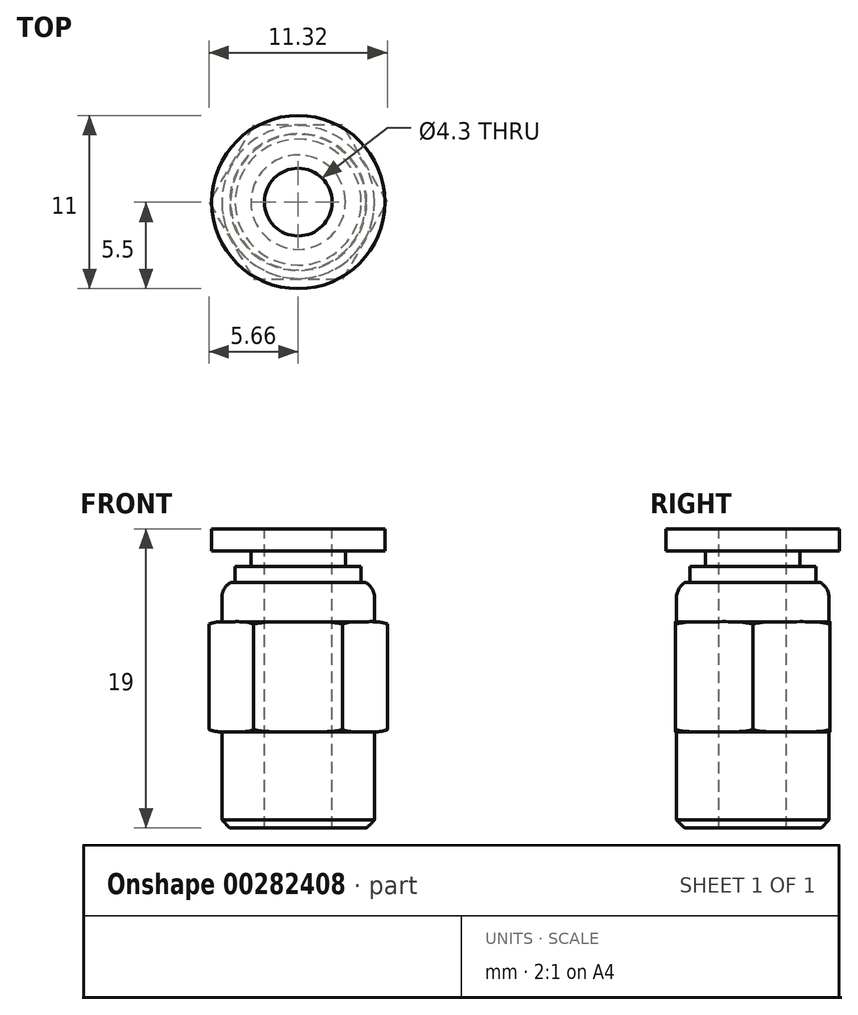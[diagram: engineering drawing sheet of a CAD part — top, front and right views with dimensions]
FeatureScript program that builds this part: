
annotation { "Feature Type Name" : "Feature", "Feature Type Description" : "" }
export const myFeature = defineFeature(function(context is Context, id is Id, definition is map)
    precondition{}
    {
        {
            var Q0;
            Q0=qCreatedBy(makeId("Front.planeOp"),FACE);
            var sketch = newSketch(context, id + "F0", { "sketchPlane" : qUnion([Q0])});
            skLineSegment(sketch, "E0", {"start": v(0, 0) * mm, "end": v(0, 19) * mm});
            skLineSegment(sketch, "E1", {"start": v(0, 19) * mm, "end": v(5.5, 19) * mm});
            skLineSegment(sketch, "E2", {"start": v(5.5, 19) * mm, "end": v(5.5, 17.6) * mm});
            skLineSegment(sketch, "E3", {"start": v(5.5, 17.6) * mm, "end": v(3, 17.6) * mm});
            skLineSegment(sketch, "E4", {"start": v(3, 17.6) * mm, "end": v(3, 16.6) * mm});
            skLineSegment(sketch, "E5", {"start": v(3, 16.6) * mm, "end": v(4, 16.6) * mm});
            skLineSegment(sketch, "E6", {"start": v(4, 16.6) * mm, "end": v(4, 15.6) * mm});
            skLineSegment(sketch, "E7", {"start": v(4, 15.6) * mm, "end": v(4.3, 15.6) * mm});
            skLineSegment(sketch, "E8", {"start": v(4.85, 14.6) * mm, "end": v(4.85, 13.1) * mm});
            skLineSegment(sketch, "E9", {"start": v(7, 11.6) * mm, "end": v(7, 7.6) * mm});
            skLineSegment(sketch, "E10", {"start": v(4.85, 6.1) * mm, "end": v(4.85, 0) * mm});
            skLineSegment(sketch, "E11", {"start": v(4.85, 0) * mm, "end": v(0, 0) * mm});
            skLineSegment(sketch, "E12", {"start": v(7, 9.6) * mm, "end": v(0, 9.6) * mm, "construction": true});
            skPoint(sketch, "E13.end.orphan", {"position": v(7, 13.1) * mm});
            skLineSegment(sketch, "E14", {"start": v(4.85, 13.1) * mm, "end": v(0, 13.1) * mm, "construction": true});
            skLineSegment(sketch, "E15", {"start": v(4.85, 6.1) * mm, "end": v(0, 6.1) * mm, "construction": true});
            skArc(sketch, "E16", {"start": v(7, 11.6) * mm, "mid": v(6.16, 12.69) * mm, "end": v(4.85, 13.1) * mm});
            skArc(sketch, "E17", {"start": v(4.85, 6.1) * mm, "mid": v(6.16, 6.51) * mm, "end": v(7, 7.6) * mm});
            skPoint(sketch, "E18.start.orphan", {"position": v(7, 6.1) * mm});
            skPoint(sketch, "E19.orphan", {"position": v(4.85, 15.6) * mm});
            skArc(sketch, "E20", {"start": v(4.85, 14.6) * mm, "mid": v(4.7, 15.17) * mm, "end": v(4.3, 15.6) * mm});
            skSolve(sketch);
        }
        {
            var Q0;
            Q0=qSketchRegion(id+"F0",true);
            var Q1;
            Q1=sQuery(id+"F0.wireOp",EDGE,"E0");
            revolve(context, id + "F1", {"entities" : qUnion([Q0]), "axis" : qUnion([Q1]), "revolveType" : RevolveType.FULL});
        }
        {
            var Q0;
            Q0=makeQuery(id+"F1.opRevolve","SWEPT_FACE",FACE,{"disambiguationData":[OSD([sQuery(id+"F0.wireOp",EDGE,"E1")])]});
            var sketch = newSketch(context, id + "F2", { "sketchPlane" : qUnion([Q0])});
            skCircle(sketch, "E21", {"center": v(0, 0) * mm, "radius": 2.15 * mm});
            skSolve(sketch);
        }
        {
            var Q0;
            Q0=qSketchRegion(id+"F2",true);
            extrude(context, id + "F3", {"entities" : qUnion([Q0]), "operationType" : NewBodyOperationType.REMOVE, "endBound" : BoundingType.THROUGH_ALL, "oppositeDirection" : true, "depth" : 25 * mm});
        }
        {
            var Q0;
            Q0=makeQuery(id+"F1.opRevolve","SWEPT_FACE",FACE,{"disambiguationData":[OSD([sQuery(id+"F0.wireOp",EDGE,"E11")])]});
            var sketch = newSketch(context, id + "F4", { "sketchPlane" : qUnion([Q0])});
            skCircle(sketch, "E22.cCircle", {"center": v(0, 0) * mm, "radius": 4.9 * mm, "construction": true});
            skLineSegment(sketch, "E22.0", {"start": v(2.83, 4.9) * mm, "end": v(5.66, 0) * mm});
            skLineSegment(sketch, "E22.1", {"start": v(5.66, 0) * mm, "end": v(2.83, -4.9) * mm});
            skLineSegment(sketch, "E22.2", {"start": v(2.83, -4.9) * mm, "end": v(-2.83, -4.9) * mm});
            skLineSegment(sketch, "E22.3", {"start": v(-2.83, -4.9) * mm, "end": v(-5.66, 0) * mm});
            skLineSegment(sketch, "E22.4", {"start": v(-5.66, 0) * mm, "end": v(-2.83, 4.9) * mm});
            skLineSegment(sketch, "E22.5", {"start": v(-2.83, 4.9) * mm, "end": v(2.83, 4.9) * mm});
            skPoint(sketch, "E22.0.midPoint", {"position": v(4.24, 2.45) * mm});
            skLineSegment(sketch, "E23", {"start": v(0, 0) * mm, "end": v(-5.66, 0) * mm, "construction": true});
            skCircle(sketch, "E24", {"center": v(0, 0) * mm, "radius": 9 * mm});
            skSolve(sketch);
        }
        {
            var Q0;
            Q0=qSketchRegion(id+"F4",true);
            extrude(context, id + "F5", {"entities" : qUnion([Q0]), "operationType" : NewBodyOperationType.REMOVE, "oppositeDirection" : true, "depth" : 14 * mm});
        }
        {
            var Q0;
            Q0=makeQuery(id+"F1.opRevolve","SWEPT_EDGE",EDGE,{"disambiguationData":[OSD([sQuery(id+"F0.wireOp",EDGE,"E10"),sQuery(id+"F0.wireOp",EDGE,"E11")])]});
            chamfer(context, id + "F6", {"entities" : qUnion([Q0]), "width" : 0.5 * mm, "tangentPropagation" : true});
        }
    });
